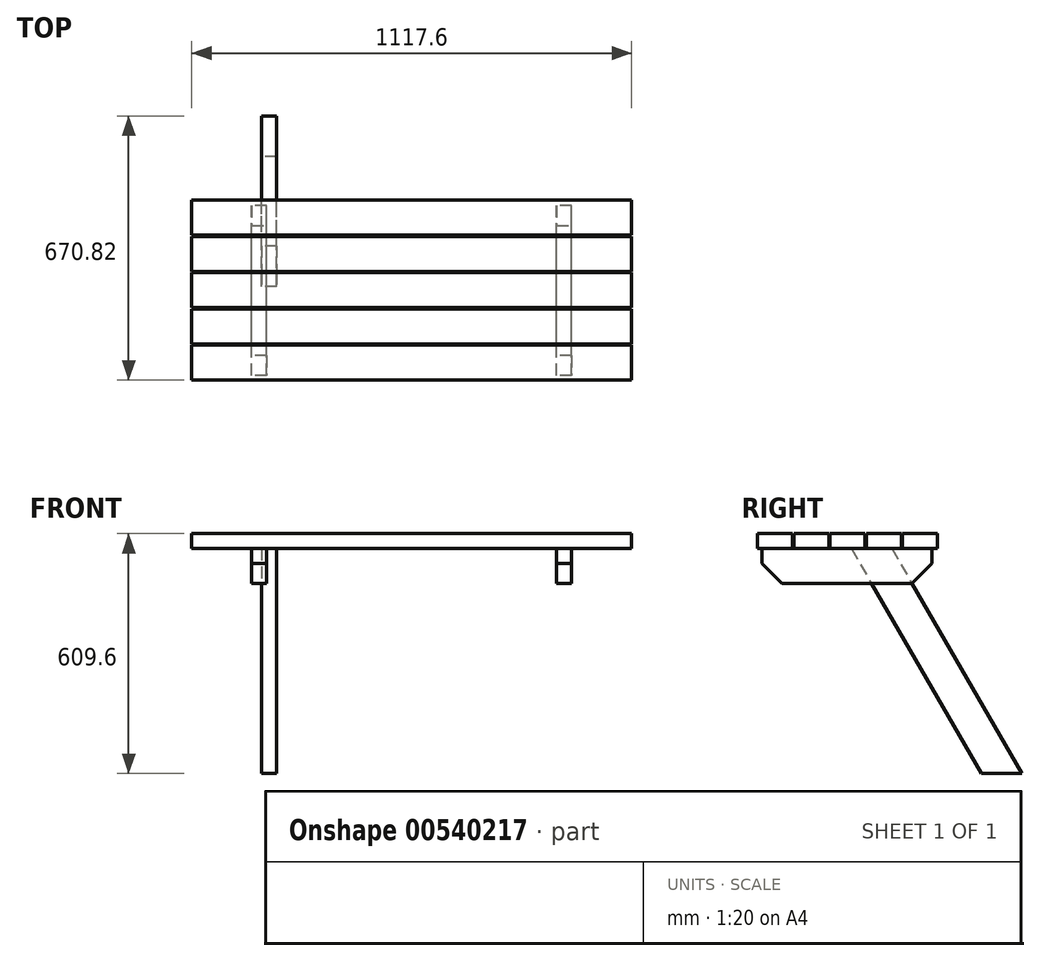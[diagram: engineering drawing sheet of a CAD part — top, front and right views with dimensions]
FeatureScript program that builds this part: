
annotation { "Feature Type Name" : "Feature", "Feature Type Description" : "" }
export const myFeature = defineFeature(function(context is Context, id is Id, definition is map)
    precondition{}
    {
        {
            var Q0;
            Q0=qCreatedBy(makeId("Top.planeOp"),FACE);
            var sketch = newSketch(context, id + "F0", { "sketchPlane" : qUnion([Q0])});
            skLineSegment(sketch, "E0.bottom", {"start": v(-177.72, 56.57) * mm, "end": v(939.88, 56.57) * mm});
            skLineSegment(sketch, "E0.top", {"start": v(-177.72, -32.33) * mm, "end": v(939.88, -32.33) * mm});
            skLineSegment(sketch, "E0.left", {"start": v(-177.72, 56.57) * mm, "end": v(-177.72, -32.33) * mm});
            skLineSegment(sketch, "E0.right", {"start": v(939.88, 56.57) * mm, "end": v(939.88, -32.33) * mm});
            skSolve(sketch);
        }
        {
            var Q0;
            Q0=makeQuery(id+"F0.imprint","IMPRINT",FACE,{"disambiguationData":[TD([[makeQuery(id+"F0.imprint","IMPRINT",EDGE,{"derivedFrom":sQuery(id+"F0.wireOp",EDGE,"E0.bottom")}),-1.0]])]});
            extrude(context, id + "F1", {"entities" : qUnion([Q0]), "depth" : 38.1 * mm, "offsetDistance" : 25.4 * mm});
        }
        {
            var Q0;
            Q0=makeQuery(id+"F1.opExtrude","SWEPT_BODY",BODY,{"disambiguationData":[OSD([sQuery(id+"F0.wireOp",EDGE,"E0.bottom"),sQuery(id+"F0.wireOp",EDGE,"E0.top"),sQuery(id+"F0.wireOp",EDGE,"E0.left"),sQuery(id+"F0.wireOp",EDGE,"E0.right")])]});
            transform(context, id + "F2", {"entities" : qUnion([Q0]), "transformType" : TransformType.TRANSLATION_3D, "dx" : 0 * mm, "dy" : 92.07 * mm, "dz" : 0 * mm, "makeCopy" : true});
        }
        {
            var Q0;
            Q0=makeQuery(id+"F2.opPattern","COPY",BODY,{"derivedFrom":makeQuery(id+"F1.opExtrude","SWEPT_BODY",BODY,{"disambiguationData":[OSD([sQuery(id+"F0.wireOp",EDGE,"E0.bottom"),sQuery(id+"F0.wireOp",EDGE,"E0.top"),sQuery(id+"F0.wireOp",EDGE,"E0.left"),sQuery(id+"F0.wireOp",EDGE,"E0.right")])]}),"instanceName":"1"});
            transform(context, id + "F3", {"entities" : qUnion([Q0]), "transformType" : TransformType.TRANSLATION_3D, "dx" : 0 * mm, "dy" : 92.07 * mm, "dz" : 0 * mm, "makeCopy" : true});
        }
        {
            var Q0;
            Q0=makeQuery(id+"F1.opExtrude","SWEPT_BODY",BODY,{"disambiguationData":[OSD([sQuery(id+"F0.wireOp",EDGE,"E0.bottom"),sQuery(id+"F0.wireOp",EDGE,"E0.top"),sQuery(id+"F0.wireOp",EDGE,"E0.left"),sQuery(id+"F0.wireOp",EDGE,"E0.right")])]});
            transform(context, id + "F4", {"entities" : qUnion([Q0]), "transformType" : TransformType.TRANSLATION_3D, "dx" : 0 * mm, "dy" : -92.07 * mm, "dz" : 0 * mm, "makeCopy" : true});
        }
        {
            var Q0;
            Q0=makeQuery(id+"F4.opPattern","COPY",BODY,{"derivedFrom":makeQuery(id+"F1.opExtrude","SWEPT_BODY",BODY,{"disambiguationData":[OSD([sQuery(id+"F0.wireOp",EDGE,"E0.bottom"),sQuery(id+"F0.wireOp",EDGE,"E0.top"),sQuery(id+"F0.wireOp",EDGE,"E0.left"),sQuery(id+"F0.wireOp",EDGE,"E0.right")])]}),"instanceName":"1"});
            transform(context, id + "F5", {"entities" : qUnion([Q0]), "transformType" : TransformType.TRANSLATION_3D, "dx" : 0 * mm, "dy" : -92.07 * mm, "dz" : 0 * mm, "makeCopy" : true});
        }
        {
            var Q0;
            Q0=qCreatedBy(makeId("Right.planeOp"),FACE);
            var sketch = newSketch(context, id + "F6", { "sketchPlane" : qUnion([Q0])});
            skLineSegment(sketch, "E1.bottom", {"start": v(-204.94, 0) * mm, "end": v(226.86, 0) * mm});
            skLineSegment(sketch, "E1.top", {"start": v(-204.94, -88.9) * mm, "end": v(226.86, -88.9) * mm});
            skLineSegment(sketch, "E1.left", {"start": v(-204.94, 0) * mm, "end": v(-204.94, -88.9) * mm});
            skLineSegment(sketch, "E1.right", {"start": v(226.86, 0) * mm, "end": v(226.86, -88.9) * mm});
            skSolve(sketch);
        }
        {
            var Q0;
            Q0 = qSketchRegion(id + "F6", true);
            extrude(context, id + "F7", {"entities" : qUnion([Q0]), "depth" : 38.1 * mm, "offsetDistance" : 25.4 * mm});
        }
        {
            var Q0;
            Q0=makeQuery(id+"F7.opExtrude","SWEPT_EDGE",EDGE,{"disambiguationData":[OSD([sQuery(id+"F6.wireOp",EDGE,"E1.top"),sQuery(id+"F6.wireOp",EDGE,"E1.right")])]});
            var Q1;
            Q1=makeQuery(id+"F7.opExtrude","SWEPT_EDGE",EDGE,{"disambiguationData":[OSD([sQuery(id+"F6.wireOp",EDGE,"E1.top"),sQuery(id+"F6.wireOp",EDGE,"E1.left")])]});
            chamfer(context, id + "F8", {"entities" : qUnion([Q0, Q1]), "width" : 50.8 * mm, "tangentPropagation" : true});
        }
        {
            var Q0;
            Q0=makeQuery(id+"F7.opExtrude","SWEPT_BODY",BODY,{"disambiguationData":[OSD([sQuery(id+"F6.wireOp",EDGE,"E1.bottom"),sQuery(id+"F6.wireOp",EDGE,"E1.top"),sQuery(id+"F6.wireOp",EDGE,"E1.left"),sQuery(id+"F6.wireOp",EDGE,"E1.right")])]});
            transform(context, id + "F9", {"entities" : qUnion([Q0]), "transformType" : TransformType.TRANSLATION_3D, "dx" : -25.4 * mm, "dy" : 0 * mm, "dz" : 0 * mm, "makeCopy" : false});
        }
        {
            var Q0;
            Q0=makeQuery(id+"F7.opExtrude","SWEPT_BODY",BODY,{"disambiguationData":[OSD([sQuery(id+"F6.wireOp",EDGE,"E1.bottom"),sQuery(id+"F6.wireOp",EDGE,"E1.top"),sQuery(id+"F6.wireOp",EDGE,"E1.left"),sQuery(id+"F6.wireOp",EDGE,"E1.right")])]});
            transform(context, id + "F10", {"entities" : qUnion([Q0]), "transformType" : TransformType.TRANSLATION_3D, "dx" : 774.7 * mm, "dy" : 0 * mm, "dz" : 0 * mm, "makeCopy" : true});
        }
        {
            var Q0;
            Q0=qCreatedBy(makeId("Right.planeOp"),FACE);
            var sketch = newSketch(context, id + "F11", { "sketchPlane" : qUnion([Q0])});
            skLineSegment(sketch, "E2", {"start": v(48.18, 0) * mm, "end": v(378.14, -571.5) * mm});
            skPoint(sketch, "E3.orphan", {"position": v(48.18, 0) * mm});
            skLineSegment(sketch, "E4", {"start": v(-54.47, 0) * mm, "end": v(275.49, -571.5) * mm});
            skLineSegment(sketch, "E5", {"start": v(48.18, 0) * mm, "end": v(-257.07, 0) * mm});
            skPoint(sketch, "E6.orphan", {"position": v(216.34, -291.25) * mm});
            skLineSegment(sketch, "E7.trimOffspring", {"start": v(275.49, -571.5) * mm, "end": v(378.14, -571.5) * mm});
            skSolve(sketch);
        }
        {
            var Q0;
            {var subQ0=sQuery(id+"F11.wireOp",EDGE,"E2");Q0=makeQuery(id+"F11.imprint","IMPRINT",FACE,{"disambiguationData":[TD([[makeQuery(id+"F11.imprint","IMPRINT",EDGE,{"derivedFrom":subQ0}),-1.0]])]});}
            extrude(context, id + "F12", {"entities" : qUnion([Q0]), "depth" : 38.1 * mm, "offsetDistance" : 25.4 * mm});
        }
        {
            var Q0;
            Q0=makeQuery(id+"F12.opExtrude","SWEPT_BODY",BODY,{"disambiguationData":[OSD([sQuery(id+"F11.wireOp",EDGE,"E2"),sQuery(id+"F11.wireOp",EDGE,"E4"),sQuery(id+"F11.wireOp",EDGE,"E5"),sQuery(id+"F11.wireOp",EDGE,"E7.trimOffspring")])]});
            transform(context, id + "F13", {"entities" : qUnion([Q0]), "transformType" : TransformType.TRANSLATION_3D, "dx" : 0 * mm, "dy" : 76.2 * mm, "dz" : 0 * mm, "makeCopy" : true});
        }
        {
            var Q0;
            Q0=makeQuery(id+"F12.opExtrude","SWEPT_BODY",BODY,{"disambiguationData":[OSD([sQuery(id+"F11.wireOp",EDGE,"E2"),sQuery(id+"F11.wireOp",EDGE,"E4"),sQuery(id+"F11.wireOp",EDGE,"E5"),sQuery(id+"F11.wireOp",EDGE,"E7.trimOffspring")])]});
            deleteBodies(context, id + "F14", {"entities" : qUnion([Q0])});
        }
        {
            var Q0;
            Q0=makeQuery(id+"F13.opPattern","COPY",BODY,{"derivedFrom":makeQuery(id+"F12.opExtrude","SWEPT_BODY",BODY,{"disambiguationData":[OSD([sQuery(id+"F11.wireOp",EDGE,"E2"),sQuery(id+"F11.wireOp",EDGE,"E4"),sQuery(id+"F11.wireOp",EDGE,"E5"),sQuery(id+"F11.wireOp",EDGE,"E7.trimOffspring")])]}),"instanceName":"1"});
            transform(context, id + "F15", {"entities" : qUnion([Q0]), "transformType" : TransformType.TRANSLATION_3D, "dx" : 0 * mm, "dy" : -127 * mm, "dz" : 0 * mm, "makeCopy" : true});
        }
        {
            var Q0;
            Q0=makeQuery(id+"F15.opPattern","COPY",BODY,{"derivedFrom":makeQuery(id+"F13.opPattern","COPY",BODY,{"derivedFrom":makeQuery(id+"F12.opExtrude","SWEPT_BODY",BODY,{"disambiguationData":[OSD([sQuery(id+"F11.wireOp",EDGE,"E2"),sQuery(id+"F11.wireOp",EDGE,"E4"),sQuery(id+"F11.wireOp",EDGE,"E5"),sQuery(id+"F11.wireOp",EDGE,"E7.trimOffspring")])]}),"instanceName":"1"}),"instanceName":"1"});
            deleteBodies(context, id + "F16", {"entities" : qUnion([Q0])});
        }
    });
